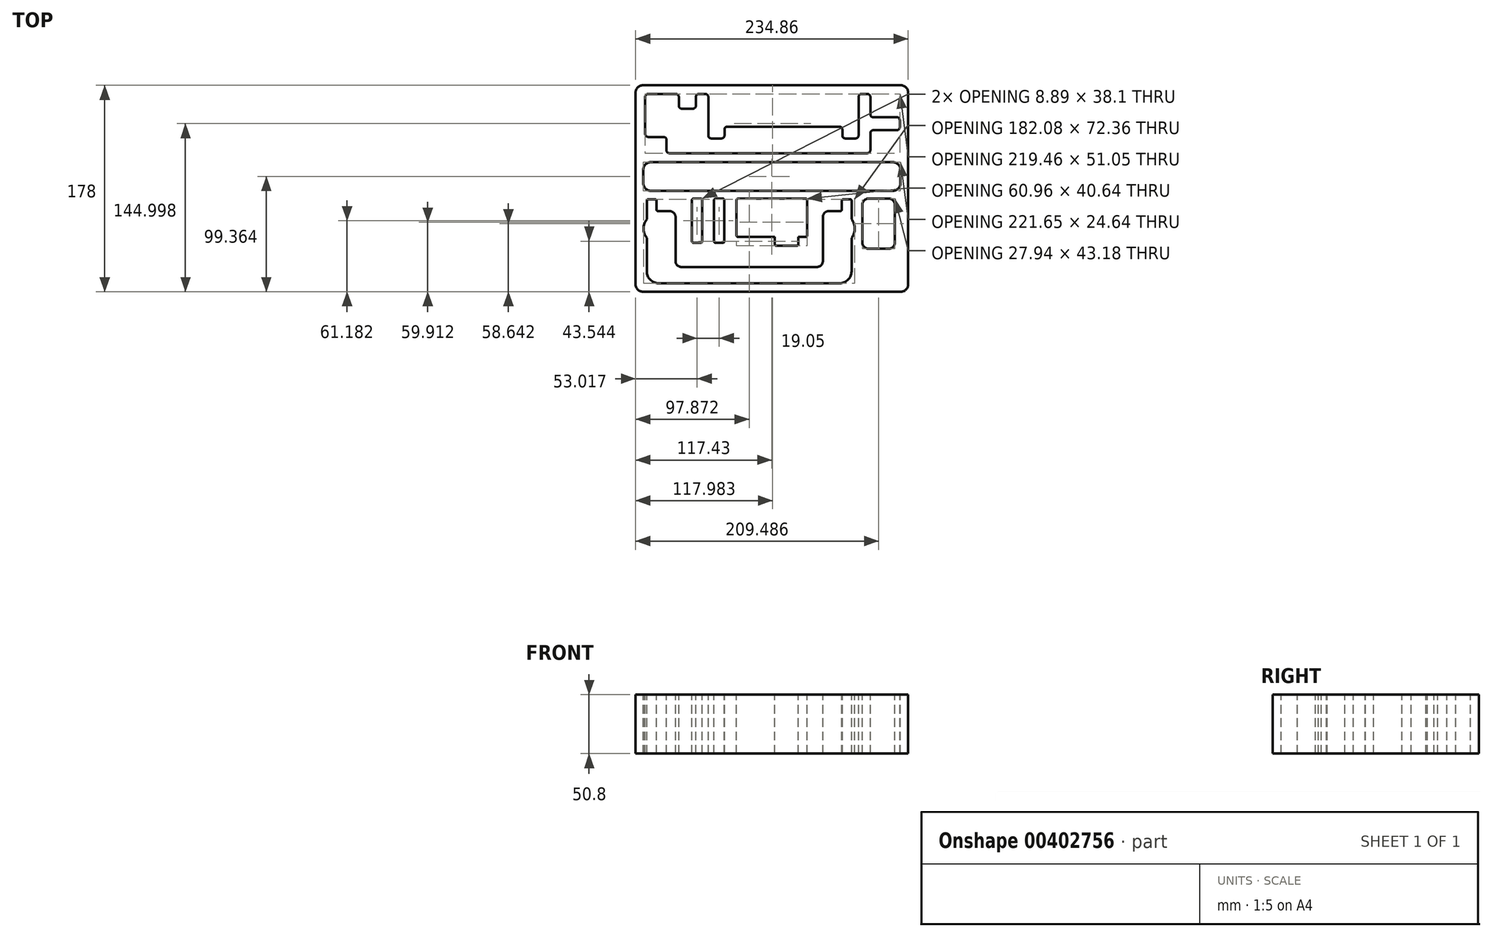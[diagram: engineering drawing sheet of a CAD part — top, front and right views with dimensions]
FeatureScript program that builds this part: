
annotation { "Feature Type Name" : "Feature", "Feature Type Description" : "" }
export const myFeature = defineFeature(function(context is Context, id is Id, definition is map)
    precondition{}
    {
        {
            var Q0;
            Q0=qCreatedBy(makeId("Top.planeOp"),FACE);
            var sketch = newSketch(context, id + "F0", { "sketchPlane" : qUnion([Q0])});
            skLineSegment(sketch, "E0", {"start": v(-117.43, 89) * mm, "end": v(117.43, -89) * mm, "construction": true});
            skLineSegment(sketch, "E1", {"start": v(-117.43, 82.9) * mm, "end": v(-117.43, -82.9) * mm});
            skLineSegment(sketch, "E2", {"start": v(-111.33, -89) * mm, "end": v(111.33, -89) * mm});
            skLineSegment(sketch, "E3", {"start": v(117.43, -82.9) * mm, "end": v(117.43, 82.9) * mm});
            skLineSegment(sketch, "E4", {"start": v(111.33, 89) * mm, "end": v(-111.33, 89) * mm});
            skPoint(sketch, "E5.visualSharp", {"position": v(-117.43, 89) * mm});
            skArc(sketch, "E5.filletArc", {"start": v(-111.33, 89) * mm, "mid": v(-115.64, 87.21) * mm, "end": v(-117.43, 82.9) * mm});
            skPoint(sketch, "E6.visualSharp", {"position": v(117.43, 89) * mm});
            skArc(sketch, "E6.filletArc", {"start": v(117.43, 82.9) * mm, "mid": v(115.64, 87.21) * mm, "end": v(111.33, 89) * mm});
            skPoint(sketch, "E7.visualSharp", {"position": v(117.43, -89) * mm});
            skArc(sketch, "E7.filletArc", {"start": v(111.33, -89) * mm, "mid": v(115.64, -87.21) * mm, "end": v(117.43, -82.9) * mm});
            skPoint(sketch, "E8.visualSharp", {"position": v(-117.43, -89) * mm});
            skArc(sketch, "E8.filletArc", {"start": v(-117.43, -82.9) * mm, "mid": v(-115.64, -87.21) * mm, "end": v(-111.33, -89) * mm});
            skLineSegment(sketch, "E9", {"start": v(0, 0) * mm, "end": v(117.43, 89) * mm, "construction": true});
            skSolve(sketch);
        }
        {
            var Q0;
            Q0 = qSketchRegion(id + "F0", true);
            extrude(context, id + "F1", {"entities" : qUnion([Q0]), "depth" : 50.8 * mm, "offsetDistance" : 25.4 * mm});
        }
        {
            var Q0;
            Q0=makeQuery(id+"F1.opExtrude","CAP_FACE",FACE,{"disambiguationData":[OSD([sQuery(id+"F0.wireOp",EDGE,"E1"),sQuery(id+"F0.wireOp",EDGE,"E2"),sQuery(id+"F0.wireOp",EDGE,"E3"),sQuery(id+"F0.wireOp",EDGE,"E4"),sQuery(id+"F0.wireOp",EDGE,"E5.filletArc"),sQuery(id+"F0.wireOp",EDGE,"E6.filletArc"),sQuery(id+"F0.wireOp",EDGE,"E7.filletArc"),sQuery(id+"F0.wireOp",EDGE,"E8.filletArc")])],"isStart":false});
            var sketch = newSketch(context, id + "F2", { "sketchPlane" : qUnion([Q0])});
            skLineSegment(sketch, "E10.bottom", {"start": v(-104.47, 22.68) * mm, "end": v(104.47, 22.68) * mm});
            skLineSegment(sketch, "E10.top", {"start": v(-104.47, -1.95) * mm, "end": v(104.47, -1.95) * mm});
            skLineSegment(sketch, "E10.left", {"start": v(-110.82, 16.33) * mm, "end": v(-110.82, 4.4) * mm});
            skLineSegment(sketch, "E10.right", {"start": v(110.82, 16.33) * mm, "end": v(110.82, 4.4) * mm});
            skPoint(sketch, "E10.middle", {"position": v(0, 10.36) * mm});
            skLineSegment(sketch, "E11", {"start": v(0, 24.24) * mm, "end": v(0, 10.36) * mm, "construction": true});
            skLineSegment(sketch, "E12.bottom", {"start": v(-104.73, 82.65) * mm, "end": v(104.73, 82.65) * mm, "construction": true});
            skLineSegment(sketch, "E12.top", {"start": v(-104.73, -82.65) * mm, "end": v(104.73, -82.65) * mm, "construction": true});
            skLineSegment(sketch, "E12.left", {"start": v(-111.08, 76.3) * mm, "end": v(-111.08, -76.3) * mm, "construction": true});
            skLineSegment(sketch, "E12.right", {"start": v(111.08, 76.3) * mm, "end": v(111.08, -76.3) * mm, "construction": true});
            skPoint(sketch, "E12.middle", {"position": v(0, 24.24) * mm});
            skPoint(sketch, "E13.visualSharp", {"position": v(-111.08, 82.65) * mm});
            skArc(sketch, "E13.filletArc", {"start": v(-104.73, 82.65) * mm, "mid": v(-109.22, 80.8) * mm, "end": v(-111.08, 76.3) * mm, "construction": true});
            skPoint(sketch, "E14.visualSharp", {"position": v(111.08, 82.65) * mm});
            skArc(sketch, "E14.filletArc", {"start": v(111.08, 76.3) * mm, "mid": v(109.22, 80.8) * mm, "end": v(104.73, 82.65) * mm, "construction": true});
            skPoint(sketch, "E15.visualSharp", {"position": v(111.08, -82.65) * mm});
            skArc(sketch, "E15.filletArc", {"start": v(104.73, -82.65) * mm, "mid": v(109.22, -80.8) * mm, "end": v(111.08, -76.3) * mm, "construction": true});
            skPoint(sketch, "E16.visualSharp", {"position": v(-111.08, -82.65) * mm});
            skArc(sketch, "E16.filletArc", {"start": v(-111.08, -76.3) * mm, "mid": v(-109.22, -80.8) * mm, "end": v(-104.73, -82.65) * mm, "construction": true});
            skPoint(sketch, "E17.visualSharp", {"position": v(-110.82, 22.68) * mm});
            skArc(sketch, "E17.filletArc", {"start": v(-104.47, 22.68) * mm, "mid": v(-108.96, 20.82) * mm, "end": v(-110.82, 16.33) * mm});
            skArc(sketch, "E18.filletArc", {"start": v(-110.82, 4.4) * mm, "mid": v(-108.96, -0.1) * mm, "end": v(-104.47, -1.95) * mm});
            skPoint(sketch, "E19.visualSharp", {"position": v(110.82, 22.68) * mm});
            skArc(sketch, "E19.filletArc", {"start": v(110.82, 16.33) * mm, "mid": v(108.96, 20.82) * mm, "end": v(104.47, 22.68) * mm});
            skPoint(sketch, "E20.visualSharp", {"position": v(110.82, -1.95) * mm});
            skArc(sketch, "E20.filletArc", {"start": v(104.47, -1.95) * mm, "mid": v(108.96, -0.1) * mm, "end": v(110.82, 4.4) * mm});
            skPoint(sketch, "E21.visualSharp", {"position": v(-90.5, 10.92) * mm});
            skLineSegment(sketch, "E22.bottom", {"start": v(-29.21, -41.79) * mm, "end": v(29.2, -41.79) * mm});
            skLineSegment(sketch, "E22.top", {"start": v(-29.21, -8.77) * mm, "end": v(29.2, -8.77) * mm});
            skLineSegment(sketch, "E22.left", {"start": v(-30.48, -40.52) * mm, "end": v(-30.48, -10.04) * mm});
            skLineSegment(sketch, "E22.right", {"start": v(30.48, -40.52) * mm, "end": v(30.48, -10.04) * mm});
            skLineSegment(sketch, "E23", {"start": v(0, -8.77) * mm, "end": v(-30.48, -25.28) * mm, "construction": true});
            skLineSegment(sketch, "E24.bottom", {"start": v(22.86, -41.79) * mm, "end": v(2.54, -41.79) * mm});
            skLineSegment(sketch, "E24.top", {"start": v(21.59, -49.4) * mm, "end": v(3.8, -49.4) * mm});
            skLineSegment(sketch, "E24.left", {"start": v(22.86, -41.79) * mm, "end": v(22.86, -48.14) * mm});
            skLineSegment(sketch, "E24.right", {"start": v(2.54, -41.79) * mm, "end": v(2.54, -48.14) * mm});
            skLineSegment(sketch, "E25.bottom", {"start": v(78.09, -13.85) * mm, "end": v(78.09, -46.87) * mm});
            skLineSegment(sketch, "E25.top", {"start": v(106.03, -13.85) * mm, "end": v(106.03, -46.87) * mm});
            skLineSegment(sketch, "E25.left", {"start": v(83.17, -8.77) * mm, "end": v(100.95, -8.77) * mm});
            skLineSegment(sketch, "E25.right", {"start": v(83.17, -51.95) * mm, "end": v(100.95, -51.95) * mm});
            skPoint(sketch, "E26.visualSharp", {"position": v(106.03, -8.77) * mm});
            skArc(sketch, "E26.filletArc", {"start": v(106.03, -13.85) * mm, "mid": v(104.54, -10.26) * mm, "end": v(100.95, -8.77) * mm});
            skPoint(sketch, "E27.visualSharp", {"position": v(78.09, -8.77) * mm});
            skArc(sketch, "E27.filletArc", {"start": v(83.17, -8.77) * mm, "mid": v(79.57, -10.26) * mm, "end": v(78.09, -13.85) * mm});
            skPoint(sketch, "E28.visualSharp", {"position": v(78.09, -51.95) * mm});
            skArc(sketch, "E28.filletArc", {"start": v(78.09, -46.87) * mm, "mid": v(79.57, -50.46) * mm, "end": v(83.17, -51.95) * mm});
            skPoint(sketch, "E29.visualSharp", {"position": v(106.03, -51.95) * mm});
            skArc(sketch, "E29.filletArc", {"start": v(100.95, -51.95) * mm, "mid": v(104.54, -50.46) * mm, "end": v(106.03, -46.87) * mm});
            skLineSegment(sketch, "E30", {"start": v(18.17, -1.95) * mm, "end": v(18.17, -8.77) * mm, "construction": true});
            skLineSegment(sketch, "E31.bottom", {"start": v(-40.92, -10.04) * mm, "end": v(-40.92, -45.6) * mm});
            skLineSegment(sketch, "E31.top", {"start": v(-49.8, -10.04) * mm, "end": v(-49.8, -45.6) * mm});
            skLineSegment(sketch, "E31.left", {"start": v(-42.19, -8.77) * mm, "end": v(-48.54, -8.77) * mm});
            skLineSegment(sketch, "E31.right", {"start": v(-42.19, -46.87) * mm, "end": v(-48.54, -46.87) * mm});
            skLineSegment(sketch, "E32", {"start": v(12.7, -49.4) * mm, "end": v(12.7, -58.4) * mm, "construction": true});
            skPoint(sketch, "E33.visualSharp", {"position": v(-30.48, -8.77) * mm});
            skArc(sketch, "E33.filletArc", {"start": v(-29.21, -8.77) * mm, "mid": v(-30.1, -9.14) * mm, "end": v(-30.48, -10.04) * mm});
            skPoint(sketch, "E34.visualSharp", {"position": v(30.48, -8.77) * mm});
            skArc(sketch, "E34.filletArc", {"start": v(30.48, -10.04) * mm, "mid": v(30.1, -9.14) * mm, "end": v(29.2, -8.77) * mm});
            skPoint(sketch, "E35.visualSharp", {"position": v(-30.48, -41.79) * mm});
            skArc(sketch, "E35.filletArc", {"start": v(-30.48, -40.52) * mm, "mid": v(-30.1, -41.42) * mm, "end": v(-29.21, -41.79) * mm});
            skPoint(sketch, "E36.visualSharp", {"position": v(30.48, -41.79) * mm});
            skArc(sketch, "E36.filletArc", {"start": v(29.2, -41.79) * mm, "mid": v(30.1, -41.42) * mm, "end": v(30.48, -40.52) * mm});
            skPoint(sketch, "E37.visualSharp", {"position": v(22.86, -49.4) * mm});
            skArc(sketch, "E37.filletArc", {"start": v(21.59, -49.4) * mm, "mid": v(22.49, -49.04) * mm, "end": v(22.86, -48.14) * mm});
            skPoint(sketch, "E38.visualSharp", {"position": v(2.54, -49.4) * mm});
            skArc(sketch, "E38.filletArc", {"start": v(2.54, -48.14) * mm, "mid": v(2.91, -49.04) * mm, "end": v(3.8, -49.4) * mm});
            skPoint(sketch, "E39.visualSharp", {"position": v(-40.92, -46.87) * mm});
            skArc(sketch, "E39.filletArc", {"start": v(-42.19, -46.87) * mm, "mid": v(-41.29, -46.5) * mm, "end": v(-40.92, -45.6) * mm});
            skPoint(sketch, "E40.visualSharp", {"position": v(-49.8, -46.87) * mm});
            skArc(sketch, "E40.filletArc", {"start": v(-49.8, -45.6) * mm, "mid": v(-49.44, -46.5) * mm, "end": v(-48.54, -46.87) * mm});
            skPoint(sketch, "E41.visualSharp", {"position": v(-49.8, -8.77) * mm});
            skArc(sketch, "E41.filletArc", {"start": v(-48.54, -8.77) * mm, "mid": v(-49.44, -9.14) * mm, "end": v(-49.8, -10.04) * mm});
            skPoint(sketch, "E42.visualSharp", {"position": v(-40.92, -8.77) * mm});
            skArc(sketch, "E42.filletArc", {"start": v(-40.92, -10.04) * mm, "mid": v(-41.29, -9.14) * mm, "end": v(-42.19, -8.77) * mm});
            skLineSegment(sketch, "E43.bottom", {"start": v(-106.64, 81.53) * mm, "end": v(-90.89, 81.53) * mm});
            skLineSegment(sketch, "E43.top", {"start": v(-106.64, 44.44) * mm, "end": v(-90.89, 44.44) * mm});
            skLineSegment(sketch, "E43.left", {"start": v(-109.18, 78.99) * mm, "end": v(-109.18, 46.98) * mm});
            skLineSegment(sketch, "E43.right", {"start": v(-90.89, 81.53) * mm, "end": v(-90.89, 44.44) * mm});
            skLineSegment(sketch, "E44.bottom", {"start": v(-90.89, 81.53) * mm, "end": v(-80.22, 81.53) * mm});
            skLineSegment(sketch, "E44.top", {"start": v(-88.35, 30.47) * mm, "end": v(-54.82, 30.47) * mm});
            skLineSegment(sketch, "E44.left", {"start": v(-90.89, 81.53) * mm, "end": v(-90.89, 33.01) * mm});
            skLineSegment(sketch, "E44.right", {"start": v(-54.82, 78.99) * mm, "end": v(-54.82, 30.47) * mm});
            skLineSegment(sketch, "E45.bottom", {"start": v(-54.82, 30.47) * mm, "end": v(74.72, 30.47) * mm});
            skLineSegment(sketch, "E45.top", {"start": v(-54.82, 43.17) * mm, "end": v(74.72, 43.17) * mm});
            skLineSegment(sketch, "E45.left", {"start": v(-54.82, 30.47) * mm, "end": v(-54.82, 43.17) * mm});
            skLineSegment(sketch, "E45.right", {"start": v(74.72, 30.47) * mm, "end": v(74.72, 43.17) * mm});
            skLineSegment(sketch, "E46.bottom", {"start": v(74.72, 30.47) * mm, "end": v(82.34, 30.47) * mm});
            skLineSegment(sketch, "E46.top", {"start": v(77.26, 81.53) * mm, "end": v(82.34, 81.53) * mm});
            skLineSegment(sketch, "E46.left", {"start": v(74.72, 30.47) * mm, "end": v(74.72, 78.99) * mm});
            skLineSegment(sketch, "E46.right", {"start": v(84.88, 33.01) * mm, "end": v(84.88, 78.99) * mm});
            skPoint(sketch, "E47.oppositeSnap0", {"position": v(84.88, 56) * mm});
            skLineSegment(sketch, "E47.bottom", {"start": v(84.88, 61.4) * mm, "end": v(107.74, 61.4) * mm});
            skLineSegment(sketch, "E47.top", {"start": v(84.88, 56) * mm, "end": v(110.28, 56) * mm});
            skLineSegment(sketch, "E47.left", {"start": v(84.88, 61.4) * mm, "end": v(84.88, 56) * mm});
            skLineSegment(sketch, "E47.right", {"start": v(110.28, 58.87) * mm, "end": v(110.28, 56) * mm});
            skLineSegment(sketch, "E48.top", {"start": v(84.88, 50.23) * mm, "end": v(107.74, 50.23) * mm});
            skLineSegment(sketch, "E48.left", {"start": v(84.88, 56) * mm, "end": v(84.88, 50.23) * mm});
            skLineSegment(sketch, "E48.right", {"start": v(110.28, 56) * mm, "end": v(110.28, 52.77) * mm});
            skPoint(sketch, "E49.visualSharp", {"position": v(-109.18, 44.44) * mm});
            skArc(sketch, "E49.filletArc", {"start": v(-109.18, 46.98) * mm, "mid": v(-108.43, 45.19) * mm, "end": v(-106.64, 44.44) * mm});
            skPoint(sketch, "E50.visualSharp", {"position": v(-109.18, 81.53) * mm});
            skArc(sketch, "E50.filletArc", {"start": v(-106.64, 81.53) * mm, "mid": v(-108.43, 80.78) * mm, "end": v(-109.18, 78.99) * mm});
            skPoint(sketch, "E51.visualSharp", {"position": v(84.88, 81.53) * mm});
            skArc(sketch, "E51.filletArc", {"start": v(84.88, 78.99) * mm, "mid": v(84.14, 80.78) * mm, "end": v(82.34, 81.53) * mm});
            skPoint(sketch, "E52.visualSharp", {"position": v(84.88, 30.47) * mm});
            skArc(sketch, "E52.filletArc", {"start": v(82.34, 30.47) * mm, "mid": v(84.14, 31.22) * mm, "end": v(84.88, 33.01) * mm});
            skPoint(sketch, "E53.visualSharp", {"position": v(110.28, 61.4) * mm});
            skArc(sketch, "E53.filletArc", {"start": v(110.28, 58.87) * mm, "mid": v(109.54, 60.67) * mm, "end": v(107.74, 61.4) * mm});
            skPoint(sketch, "E54.visualSharp", {"position": v(110.28, 50.23) * mm});
            skArc(sketch, "E54.filletArc", {"start": v(107.74, 50.23) * mm, "mid": v(109.54, 50.98) * mm, "end": v(110.28, 52.77) * mm});
            skPoint(sketch, "E55.visualSharp", {"position": v(74.72, 81.53) * mm});
            skArc(sketch, "E55.filletArc", {"start": v(77.26, 81.53) * mm, "mid": v(75.46, 80.78) * mm, "end": v(74.72, 78.99) * mm});
            skPoint(sketch, "E56.visualSharp", {"position": v(-54.82, 81.53) * mm});
            skArc(sketch, "E56.filletArc", {"start": v(-54.82, 78.99) * mm, "mid": v(-55.56, 80.78) * mm, "end": v(-57.36, 81.53) * mm});
            skPoint(sketch, "E57.visualSharp", {"position": v(-90.89, 30.47) * mm});
            skArc(sketch, "E57.filletArc", {"start": v(-90.89, 33.01) * mm, "mid": v(-90.14, 31.22) * mm, "end": v(-88.35, 30.47) * mm});
            skLineSegment(sketch, "E58.bottom", {"start": v(-40.85, 43.17) * mm, "end": v(60.75, 43.17) * mm});
            skLineSegment(sketch, "E58.top", {"start": v(-38.3, 53.33) * mm, "end": v(58.21, 53.33) * mm});
            skLineSegment(sketch, "E58.left", {"start": v(-40.85, 43.17) * mm, "end": v(-40.85, 50.8) * mm});
            skLineSegment(sketch, "E58.right", {"start": v(60.75, 43.17) * mm, "end": v(60.75, 50.8) * mm});
            skLineSegment(sketch, "E59", {"start": v(-54.82, 47.67) * mm, "end": v(-40.85, 47.67) * mm, "construction": true});
            skLineSegment(sketch, "E60", {"start": v(-40.85, 47.67) * mm, "end": v(60.75, 47.67) * mm, "construction": true});
            skLineSegment(sketch, "E61", {"start": v(60.75, 47.67) * mm, "end": v(74.72, 47.67) * mm, "construction": true});
            skPoint(sketch, "E62.visualSharp", {"position": v(-40.85, 53.33) * mm});
            skArc(sketch, "E62.filletArc", {"start": v(-38.3, 53.33) * mm, "mid": v(-40.1, 52.59) * mm, "end": v(-40.85, 50.8) * mm});
            skPoint(sketch, "E63.visualSharp", {"position": v(60.75, 53.33) * mm});
            skArc(sketch, "E63.filletArc", {"start": v(60.75, 50.8) * mm, "mid": v(60, 52.59) * mm, "end": v(58.21, 53.33) * mm});
            skLineSegment(sketch, "E64.top", {"start": v(-68.03, 68.83) * mm, "end": v(-77.68, 68.83) * mm});
            skLineSegment(sketch, "E64.left", {"start": v(-65.49, 81.53) * mm, "end": v(-65.49, 71.37) * mm});
            skLineSegment(sketch, "E64.right", {"start": v(-80.22, 81.53) * mm, "end": v(-80.22, 71.37) * mm});
            skPoint(sketch, "E65.visualSharp", {"position": v(-65.49, 68.83) * mm});
            skArc(sketch, "E65.filletArc", {"start": v(-68.03, 68.83) * mm, "mid": v(-66.23, 69.57) * mm, "end": v(-65.49, 71.37) * mm});
            skPoint(sketch, "E66.visualSharp", {"position": v(-80.22, 68.83) * mm});
            skArc(sketch, "E66.filletArc", {"start": v(-80.22, 71.37) * mm, "mid": v(-79.48, 69.57) * mm, "end": v(-77.68, 68.83) * mm});
            skLineSegment(sketch, "E67.trimOffspring", {"start": v(-65.49, 81.53) * mm, "end": v(-57.36, 81.53) * mm});
            skLineSegment(sketch, "E68", {"start": v(-58.95, 4.06) * mm, "end": v(-58.95, -55.47) * mm, "construction": true});
            skArc(sketch, "E69.MirrorCS", {"start": v(-59.97, -45.6) * mm, "mid": v(-60.34, -46.5) * mm, "end": v(-61.24, -46.87) * mm});
            skArc(sketch, "E70.MirrorCS", {"start": v(-68.86, -10.04) * mm, "mid": v(-68.49, -9.14) * mm, "end": v(-67.59, -8.77) * mm});
            skArc(sketch, "E71.MirrorCS", {"start": v(-61.24, -8.77) * mm, "mid": v(-60.34, -9.14) * mm, "end": v(-59.97, -10.04) * mm});
            skArc(sketch, "E72.MirrorCS", {"start": v(-67.59, -46.87) * mm, "mid": v(-68.49, -46.5) * mm, "end": v(-68.86, -45.6) * mm});
            skLineSegment(sketch, "E73.MirrorCS", {"start": v(-67.59, -46.87) * mm, "end": v(-61.24, -46.87) * mm});
            skPoint(sketch, "E74.MirrorP", {"position": v(-68.86, -8.44) * mm});
            skPoint(sketch, "E75.MirrorP", {"position": v(-59.97, -8.44) * mm});
            skPoint(sketch, "E76.MirrorP", {"position": v(-59.97, -46.54) * mm});
            skPoint(sketch, "E77.MirrorP", {"position": v(-68.86, -46.54) * mm});
            skLineSegment(sketch, "E78.MirrorCS", {"start": v(-67.59, -8.77) * mm, "end": v(-61.24, -8.77) * mm});
            skLineSegment(sketch, "E79.MirrorCS", {"start": v(-68.86, -10.04) * mm, "end": v(-68.86, -45.6) * mm});
            skLineSegment(sketch, "E80.MirrorCS", {"start": v(-59.97, -10.04) * mm, "end": v(-59.97, -45.6) * mm});
            skSolve(sketch);
        }
        {
            var Q0;
            Q0 = qSketchRegion(id + "F2", true);
            extrude(context, id + "F3", {"entities" : qUnion([Q0]), "operationType" : NewBodyOperationType.REMOVE, "oppositeDirection" : true, "depth" : 50.8 * mm, "offsetDistance" : 25.4 * mm});
        }
        {
            var Q0;
            Q0=makeQuery(id+"F3.boolean.opBoolean","COPY",EDGE,{"derivedFrom":makeQuery(id+"F3.opExtrude","SWEPT_EDGE",EDGE,{"disambiguationData":[OSD([sQuery(id+"F2.wireOp",EDGE,"E44.right"),sQuery(id+"F2.wireOp",EDGE,"E45.top"),sQuery(id+"F2.wireOp",EDGE,"E45.left")])]})});
            var Q1;
            Q1=makeQuery(id+"F3.boolean.opBoolean","COPY",EDGE,{"derivedFrom":makeQuery(id+"F3.opExtrude","SWEPT_EDGE",EDGE,{"disambiguationData":[OSD([sQuery(id+"F2.wireOp",EDGE,"E45.top"),sQuery(id+"F2.wireOp",EDGE,"E46.left")])]})});
            var Q2;
            Q2=makeQuery(id+"F3.boolean.opBoolean","COPY",EDGE,{"derivedFrom":makeQuery(id+"F3.opExtrude","SWEPT_EDGE",EDGE,{"disambiguationData":[OSD([sQuery(id+"F2.wireOp",EDGE,"E46.right"),sQuery(id+"F2.wireOp",EDGE,"E48.top"),sQuery(id+"F2.wireOp",EDGE,"E48.left")])]})});
            var Q3;
            Q3=makeQuery(id+"F3.boolean.opBoolean","COPY",EDGE,{"derivedFrom":makeQuery(id+"F3.opExtrude","SWEPT_EDGE",EDGE,{"disambiguationData":[OSD([sQuery(id+"F2.wireOp",EDGE,"E46.right"),sQuery(id+"F2.wireOp",EDGE,"E47.bottom"),sQuery(id+"F2.wireOp",EDGE,"E47.left")])]})});
            var Q4;
            Q4=makeQuery(id+"F3.boolean.opBoolean","COPY",EDGE,{"derivedFrom":makeQuery(id+"F3.opExtrude","SWEPT_EDGE",EDGE,{"disambiguationData":[OSD([sQuery(id+"F2.wireOp",EDGE,"E43.top"),sQuery(id+"F2.wireOp",EDGE,"E44.left")])]})});
            fillet(context, id + "F4", {"entities" : qUnion([Q0, Q1, Q2, Q3, Q4]), "radius" : 2.54 * mm, "tangentPropagation" : true, "allowEdgeOverflow" : false});
        }
        {
            var Q0;
            Q0=makeQuery(id+"F3.boolean.opBoolean","COPY",EDGE,{"derivedFrom":makeQuery(id+"F3.opExtrude","SWEPT_EDGE",EDGE,{"disambiguationData":[OSD([sQuery(id+"F2.wireOp",EDGE,"E45.top"),sQuery(id+"F2.wireOp",EDGE,"E58.bottom"),sQuery(id+"F2.wireOp",EDGE,"E58.left")])]})});
            var Q1;
            Q1=makeQuery(id+"F3.boolean.opBoolean","COPY",EDGE,{"derivedFrom":makeQuery(id+"F3.opExtrude","SWEPT_EDGE",EDGE,{"disambiguationData":[OSD([sQuery(id+"F2.wireOp",EDGE,"E45.top"),sQuery(id+"F2.wireOp",EDGE,"E58.bottom"),sQuery(id+"F2.wireOp",EDGE,"E58.right")])]})});
            fillet(context, id + "F5", {"entities" : qUnion([Q0, Q1]), "radius" : 2.54 * mm, "tangentPropagation" : true, "allowEdgeOverflow" : false});
        }
        {
            var Q0;
            Q0=makeQuery(id+"F3.boolean.opBoolean","COPY",EDGE,{"derivedFrom":makeQuery(id+"F3.opExtrude","SWEPT_EDGE",EDGE,{"disambiguationData":[OSD([sQuery(id+"F2.wireOp",EDGE,"E44.bottom"),sQuery(id+"F2.wireOp",EDGE,"E64.right")])]})});
            var Q1;
            Q1=makeQuery(id+"F3.boolean.opBoolean","COPY",EDGE,{"derivedFrom":makeQuery(id+"F3.opExtrude","SWEPT_EDGE",EDGE,{"disambiguationData":[OSD([sQuery(id+"F2.wireOp",EDGE,"E64.left"),sQuery(id+"F2.wireOp",EDGE,"E67.trimOffspring")])]})});
            fillet(context, id + "F6", {"entities" : qUnion([Q0, Q1]), "radius" : 2.54 * mm, "tangentPropagation" : true, "allowEdgeOverflow" : false});
        }
        {
            var Q0;
            Q0=makeQuery(id+"F1.opExtrude","CAP_FACE",FACE,{"disambiguationData":[OSD([sQuery(id+"F0.wireOp",EDGE,"E1"),sQuery(id+"F0.wireOp",EDGE,"E2"),sQuery(id+"F0.wireOp",EDGE,"E3"),sQuery(id+"F0.wireOp",EDGE,"E4"),sQuery(id+"F0.wireOp",EDGE,"E5.filletArc"),sQuery(id+"F0.wireOp",EDGE,"E6.filletArc"),sQuery(id+"F0.wireOp",EDGE,"E7.filletArc"),sQuery(id+"F0.wireOp",EDGE,"E8.filletArc")])],"isStart":false});
            var sketch = newSketch(context, id + "F7", { "sketchPlane" : qUnion([Q0])});
            skLineSegment(sketch, "E81", {"start": v(-19.56, -68.93) * mm, "end": v(-19.56, -58.78) * mm, "construction": true});
            skLineSegment(sketch, "E82", {"start": v(-19.56, -67.66) * mm, "end": v(-64.96, -67.66) * mm});
            skLineSegment(sketch, "E83", {"start": v(-64.96, -67.66) * mm, "end": v(-77.98, -67.66) * mm});
            skLineSegment(sketch, "E84", {"start": v(-83.06, -62.58) * mm, "end": v(-83.06, -42.26) * mm});
            skLineSegment(sketch, "E85", {"start": v(-86.87, -38.45) * mm, "end": v(-86.87, -38.45) * mm});
            skLineSegment(sketch, "E86", {"start": v(-91.95, -19.47) * mm, "end": v(-98.23, -19.47) * mm});
            skLineSegment(sketch, "E87", {"start": v(-103.38, -9.28) * mm, "end": v(-106.55, -9.28) * mm});
            skLineSegment(sketch, "E88", {"start": v(-107.82, -10.55) * mm, "end": v(-107.82, -71.47) * mm});
            skLineSegment(sketch, "E89", {"start": v(-97.66, -81.63) * mm, "end": v(-19.56, -81.63) * mm});
            skPoint(sketch, "E90.visualSharp", {"position": v(-83.06, -67.66) * mm});
            skArc(sketch, "E90.filletArc", {"start": v(-83.06, -62.58) * mm, "mid": v(-81.57, -66.18) * mm, "end": v(-77.98, -67.66) * mm});
            skPoint(sketch, "E91.visualSharp", {"position": v(-107.82, -9.28) * mm});
            skArc(sketch, "E91.filletArc", {"start": v(-106.55, -9.28) * mm, "mid": v(-107.45, -9.65) * mm, "end": v(-107.82, -10.55) * mm});
            skPoint(sketch, "E92.visualSharp", {"position": v(-107.82, -81.63) * mm});
            skArc(sketch, "E92.filletArc", {"start": v(-107.82, -71.47) * mm, "mid": v(-104.85, -78.66) * mm, "end": v(-97.66, -81.63) * mm});
            skLineSegment(sketch, "E93", {"start": v(-99.5, -18.2) * mm, "end": v(-99.5, -10.55) * mm});
            skLineSegment(sketch, "E94", {"start": v(-100.77, -9.28) * mm, "end": v(-103.38, -9.28) * mm});
            skPoint(sketch, "E95.visualSharp", {"position": v(-99.5, -19.47) * mm});
            skArc(sketch, "E95.filletArc", {"start": v(-99.5, -18.2) * mm, "mid": v(-99.13, -19.1) * mm, "end": v(-98.23, -19.47) * mm});
            skPoint(sketch, "E96.visualSharp", {"position": v(-99.5, -9.28) * mm});
            skArc(sketch, "E96.filletArc", {"start": v(-99.5, -10.55) * mm, "mid": v(-99.87, -9.65) * mm, "end": v(-100.77, -9.28) * mm});
            skArc(sketch, "E97.MirrorCS", {"start": v(-107.82, -42.62) * mm, "mid": v(-110.6, -34.6) * mm, "end": v(-107.82, -26.6) * mm});
            skLineSegment(sketch, "E98", {"start": v(-83.06, -42.26) * mm, "end": v(-83.06, -24.55) * mm});
            skLineSegment(sketch, "E99", {"start": v(-88.14, -19.47) * mm, "end": v(-91.95, -19.47) * mm});
            skPoint(sketch, "E100.visualSharp", {"position": v(-83.06, -19.47) * mm});
            skArc(sketch, "E100.filletArc", {"start": v(-83.06, -24.55) * mm, "mid": v(-84.55, -20.95) * mm, "end": v(-88.14, -19.47) * mm});
            skLineSegment(sketch, "E101.MirrorCS", {"start": v(64.26, -9.28) * mm, "end": v(67.44, -9.28) * mm});
            skArc(sketch, "E102.MirrorCS", {"start": v(67.44, -9.28) * mm, "mid": v(68.34, -9.65) * mm, "end": v(68.7, -10.55) * mm});
            skLineSegment(sketch, "E103.MirrorCS", {"start": v(61.66, -9.28) * mm, "end": v(64.26, -9.28) * mm});
            skArc(sketch, "E104.MirrorCS", {"start": v(60.39, -18.2) * mm, "mid": v(60.01, -19.1) * mm, "end": v(59.12, -19.47) * mm});
            skArc(sketch, "E105.MirrorCS", {"start": v(60.39, -10.55) * mm, "mid": v(60.76, -9.65) * mm, "end": v(61.66, -9.28) * mm});
            skLineSegment(sketch, "E106.MirrorCS", {"start": v(49.02, -19.47) * mm, "end": v(52.83, -19.47) * mm});
            skLineSegment(sketch, "E107.MirrorCS", {"start": v(52.83, -19.47) * mm, "end": v(59.12, -19.47) * mm});
            skArc(sketch, "E108.MirrorCS", {"start": v(43.94, -62.58) * mm, "mid": v(42.45, -66.18) * mm, "end": v(38.86, -67.66) * mm});
            skArc(sketch, "E109.MirrorCS", {"start": v(43.94, -24.55) * mm, "mid": v(45.43, -20.95) * mm, "end": v(49.02, -19.47) * mm});
            skLineSegment(sketch, "E110.MirrorCS", {"start": v(68.7, -10.55) * mm, "end": v(68.7, -71.47) * mm});
            skLineSegment(sketch, "E111.MirrorCS", {"start": v(43.94, -42.26) * mm, "end": v(43.94, -24.55) * mm});
            skLineSegment(sketch, "E112.MirrorCS", {"start": v(58.55, -81.63) * mm, "end": v(-19.56, -81.63) * mm});
            skPoint(sketch, "E113.MirrorP", {"position": v(68.7, -81.63) * mm});
            skArc(sketch, "E114.MirrorCS", {"start": v(68.7, -71.47) * mm, "mid": v(65.73, -78.66) * mm, "end": v(58.55, -81.63) * mm});
            skLineSegment(sketch, "E115.MirrorCS", {"start": v(60.39, -18.2) * mm, "end": v(60.39, -10.55) * mm});
            skPoint(sketch, "E116.MirrorP", {"position": v(60.39, -9.28) * mm});
            skPoint(sketch, "E117.MirrorP", {"position": v(68.7, -9.28) * mm});
            skPoint(sketch, "E118.MirrorP", {"position": v(43.94, -19.47) * mm});
            skPoint(sketch, "E119.MirrorP", {"position": v(60.39, -19.47) * mm});
            skPoint(sketch, "E120.MirrorP", {"position": v(43.94, -67.66) * mm});
            skArc(sketch, "E121.MirrorCS", {"start": v(68.7, -42.62) * mm, "mid": v(71.48, -34.6) * mm, "end": v(68.7, -26.6) * mm});
            skLineSegment(sketch, "E122.MirrorCS", {"start": v(-19.56, -67.66) * mm, "end": v(25.85, -67.66) * mm});
            skLineSegment(sketch, "E123.MirrorCS", {"start": v(43.94, -62.58) * mm, "end": v(43.94, -42.26) * mm});
            skLineSegment(sketch, "E124.MirrorCS", {"start": v(25.85, -67.66) * mm, "end": v(38.86, -67.66) * mm});
            skSolve(sketch);
        }
        {
            var Q0;
            Q0 = qSketchRegion(id + "F7", true);
            extrude(context, id + "F8", {"entities" : qUnion([Q0]), "operationType" : NewBodyOperationType.REMOVE, "oppositeDirection" : true, "depth" : 50.8 * mm, "offsetDistance" : 25.4 * mm});
        }
    });
